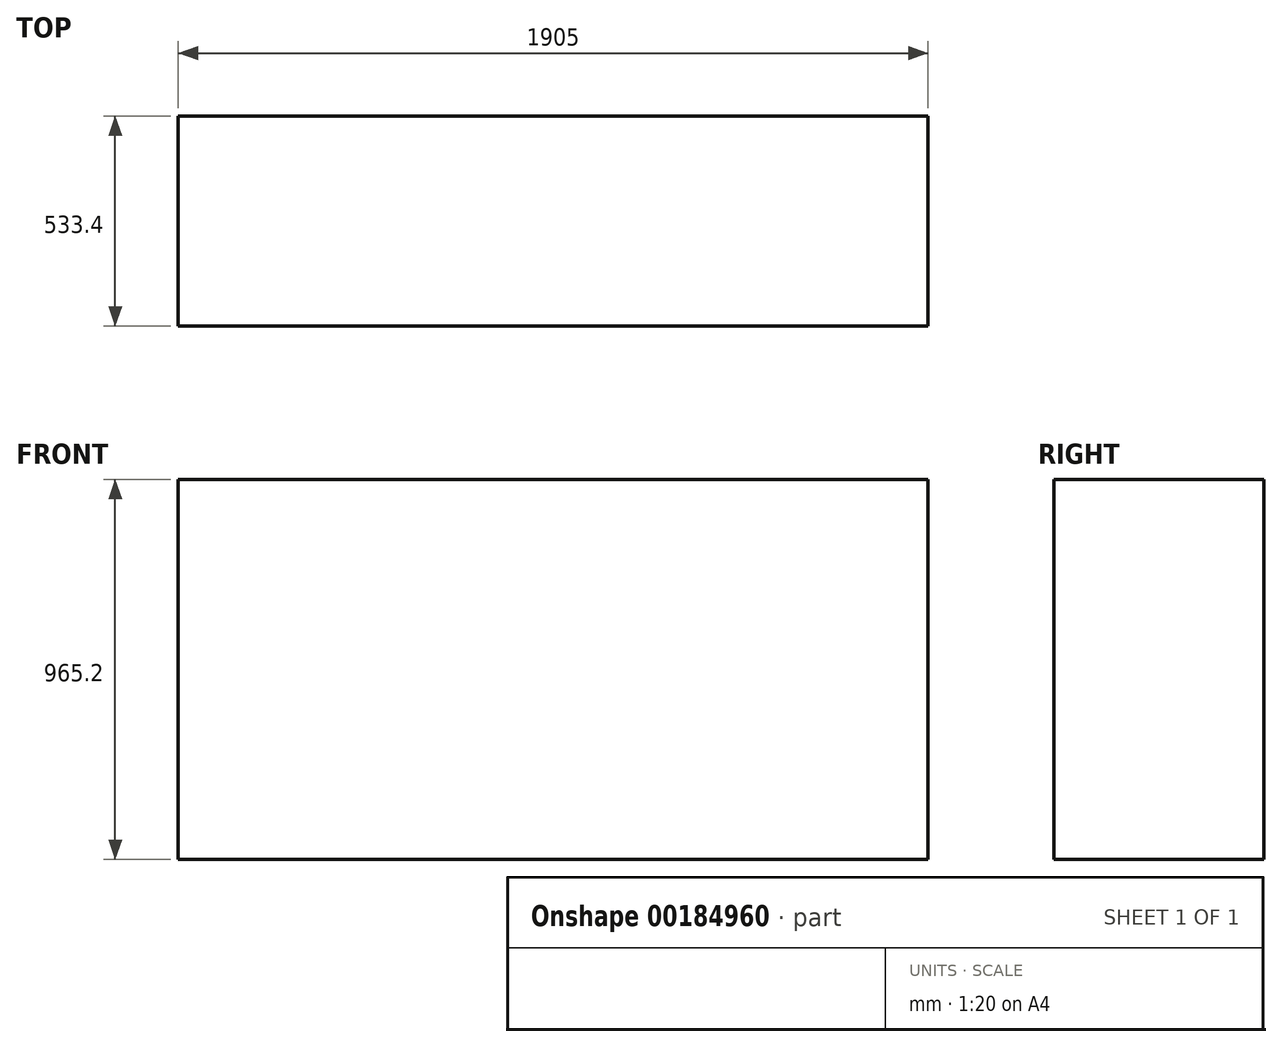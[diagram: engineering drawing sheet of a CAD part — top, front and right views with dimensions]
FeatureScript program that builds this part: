
annotation { "Feature Type Name" : "Feature", "Feature Type Description" : "" }
export const myFeature = defineFeature(function(context is Context, id is Id, definition is map)
    precondition{}
    {
        {
            var Q0;
            Q0=qCreatedBy(makeId("Top.planeOp"),FACE);
            var sketch = newSketch(context, id + "F0", { "sketchPlane" : qUnion([Q0])});
            skLineSegment(sketch, "E0.bottom", {"start": v(952.5, 266.7) * mm, "end": v(-952.5, 266.7) * mm});
            skLineSegment(sketch, "E0.top", {"start": v(952.5, -266.7) * mm, "end": v(-952.5, -266.7) * mm});
            skLineSegment(sketch, "E0.left", {"start": v(952.5, 266.7) * mm, "end": v(952.5, -266.7) * mm});
            skLineSegment(sketch, "E0.right", {"start": v(-952.5, 266.7) * mm, "end": v(-952.5, -266.7) * mm});
            skPoint(sketch, "E0.middle", {"position": v(0, 0) * mm});
            skSolve(sketch);
        }
        {
            var Q0;
            Q0=makeQuery(id+"F0.imprint","IMPRINT",FACE,{"disambiguationData":[TD([[makeQuery(id+"F0.imprint","IMPRINT",EDGE,{"derivedFrom":sQuery(id+"F0.wireOp",EDGE,"E0.bottom")}),1.0]])]});
            extrude(context, id + "F1", {"entities" : qUnion([Q0]), "depth" : 965.2 * mm});
        }
    });
